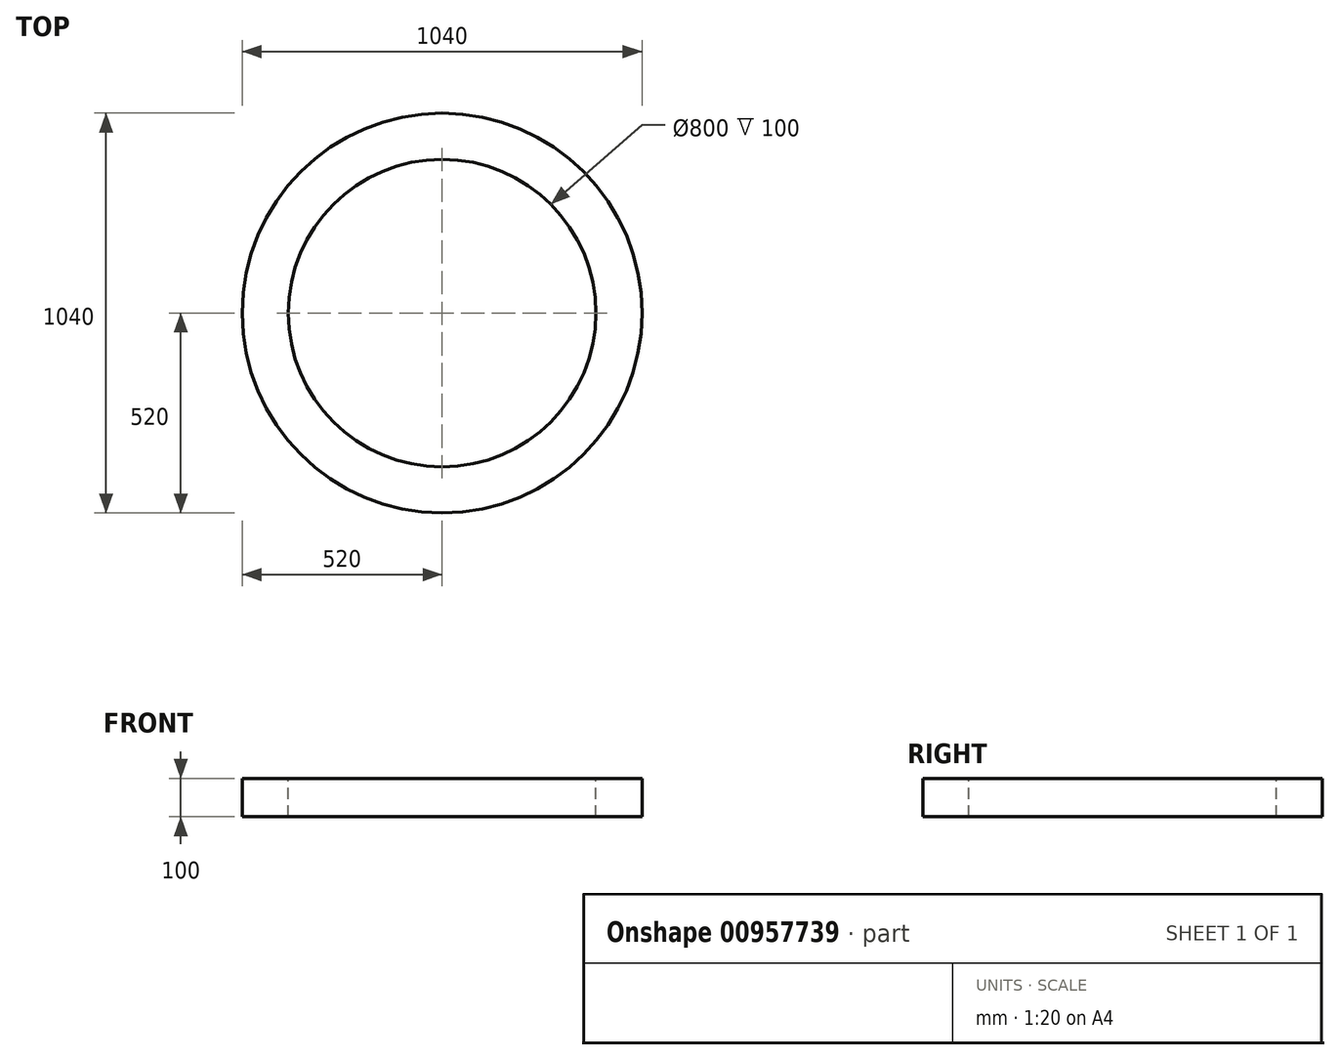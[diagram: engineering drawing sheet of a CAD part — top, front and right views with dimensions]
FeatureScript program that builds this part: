
annotation { "Feature Type Name" : "Feature", "Feature Type Description" : "" }
export const myFeature = defineFeature(function(context is Context, id is Id, definition is map)
    precondition{}
    {
        {
            var Q0;
            Q0=qCreatedBy(makeId("Front.planeOp"),FACE);
            var sketch = newSketch(context, id + "F0", { "sketchPlane" : qUnion([Q0])});
            skLineSegment(sketch, "E0.bottom", {"start": v(-520, 100) * mm, "end": v(-400, 100) * mm});
            skLineSegment(sketch, "E0.top", {"start": v(-520, 0) * mm, "end": v(-400, 0) * mm});
            skLineSegment(sketch, "E0.left", {"start": v(-520, 100) * mm, "end": v(-520, 0) * mm});
            skLineSegment(sketch, "E0.right", {"start": v(-400, 100) * mm, "end": v(-400, 0) * mm});
            skSolve(sketch);
        }
        {
            var Q0;
            Q0=qCreatedBy(makeId("Front.planeOp"),FACE);
            var sketch = newSketch(context, id + "F1", { "sketchPlane" : qUnion([Q0])});
            skLineSegment(sketch, "E1", {"start": v(0, 0) * mm, "end": v(0, 102.24) * mm, "construction": true});
            skSolve(sketch);
        }
        {
            var Q0;
            Q0=qSketchRegion(id+"F0",true);
            var Q1;
            Q1=sQuery(id+"F1.wireOp",EDGE,"E1");
            revolve(context, id + "F2", {"surfaceOperationType" : NewSurfaceOperationType.NEW, "entities" : qUnion([Q0]), "axis" : qUnion([Q1]), "revolveType" : RevolveType.FULL, "oppositeDirection" : true});
        }
    });
